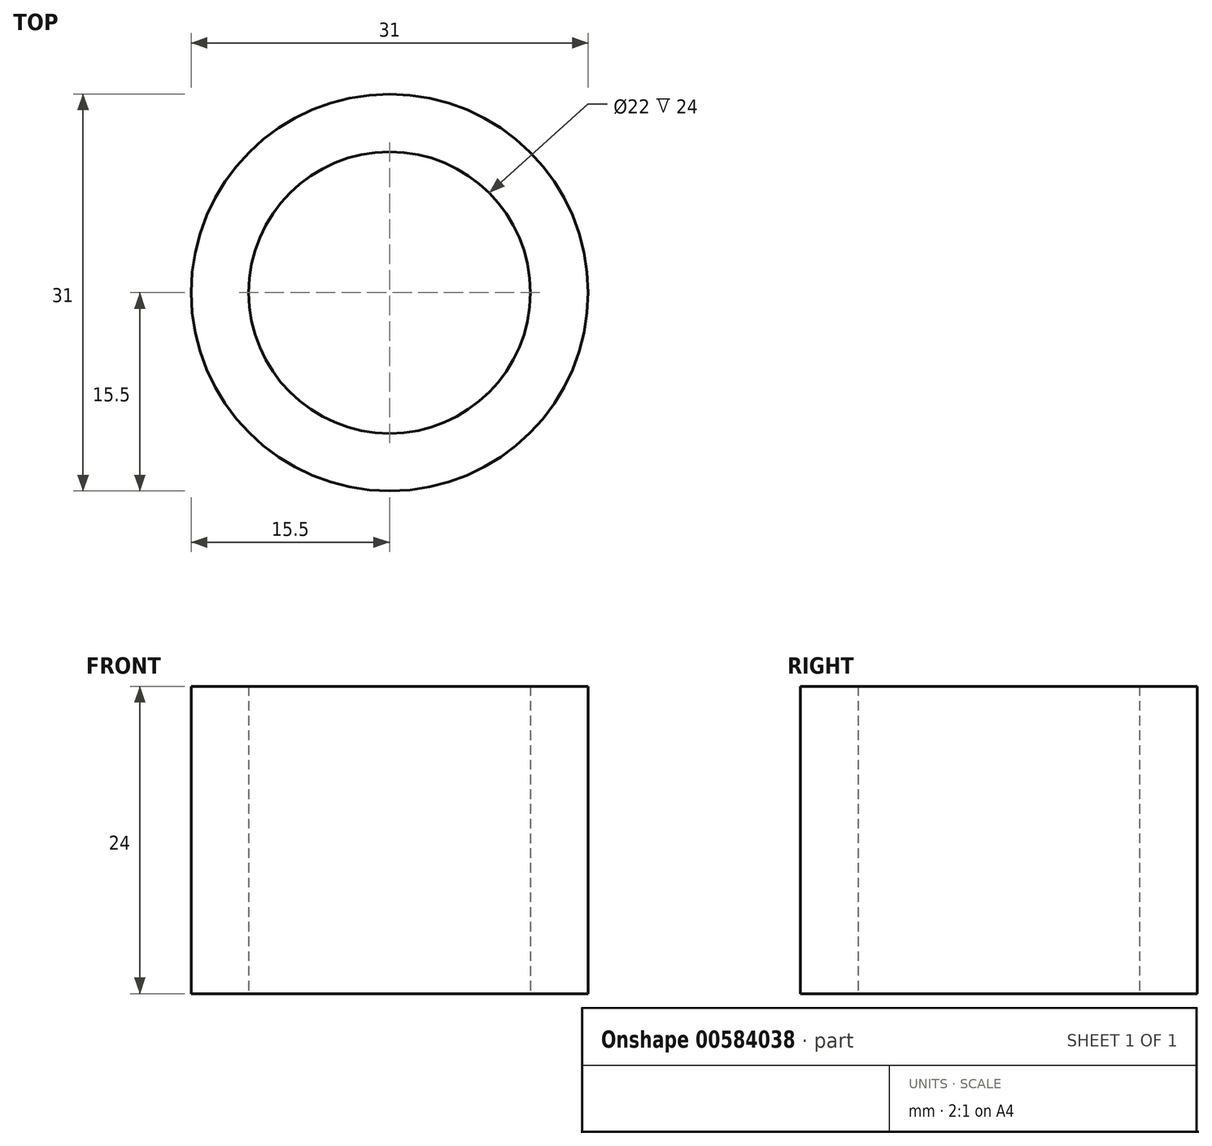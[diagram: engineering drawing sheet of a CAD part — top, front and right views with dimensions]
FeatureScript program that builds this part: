
annotation { "Feature Type Name" : "Feature", "Feature Type Description" : "" }
export const myFeature = defineFeature(function(context is Context, id is Id, definition is map)
    precondition{}
    {
        {
            var Q0;
            Q0=qCreatedBy(makeId("Top.planeOp"),FACE);
            var sketch = newSketch(context, id + "F0", { "sketchPlane" : qUnion([Q0])});
            skCircle(sketch, "E0", {"center": v(0, 0) * mm, "radius": 11 * mm});
            skCircle(sketch, "E1", {"center": v(0, 0) * mm, "radius": 15.5 * mm});
            skPoint(sketch, "E2.middle", {"position": v(-11, 0) * mm});
            skCircle(sketch, "E3", {"center": v(0, 0) * mm, "radius": 11.75 * mm});
            skLineSegment(sketch, "E4", {"start": v(-11, 0) * mm, "end": v(-11.75, 0) * mm});
            skLineSegment(sketch, "E5", {"start": v(11, 0) * mm, "end": v(11.75, 0) * mm});
            skLineSegment(sketch, "E6", {"start": v(0, 11) * mm, "end": v(0, 11.75) * mm});
            skLineSegment(sketch, "E7", {"start": v(0, -11.75) * mm, "end": v(0, -11) * mm});
            skSolve(sketch);
        }
        {
            var Q0;
            Q0=makeQuery(id+"F0.imprint","IMPRINT",FACE,{"disambiguationData":[TD([[makeQuery(id+"F0.imprint","IMPRINT",EDGE,{"derivedFrom":sQuery(id+"F0.wireOp",EDGE,"E0")}),-1.0]])]});
            var Q1;
            Q1=makeQuery(id+"F0.imprint","IMPRINT",FACE,{"disambiguationData":[TD([[makeQuery(id+"F0.imprint","IMPRINT",EDGE,{"derivedFrom":sQuery(id+"F0.wireOp",EDGE,"E1")}),1.0]])]});
            extrude(context, id + "F1", {"entities" : qUnion([Q0, Q1]), "depth" : 24 * mm, "offsetDistance" : 25 * mm});
        }
        {
            var Q0;
            Q0=qCreatedBy(makeId("Front.planeOp"),FACE);
            cPlane(context, id + "F2", {"entities" : qUnion([Q0]), "cplaneType" : CPlaneType.OFFSET, "offset" : 11 * mm, "oppositeDirection" : true, "width" : 150 * mm, "height" : 150 * mm});
        }
    });
